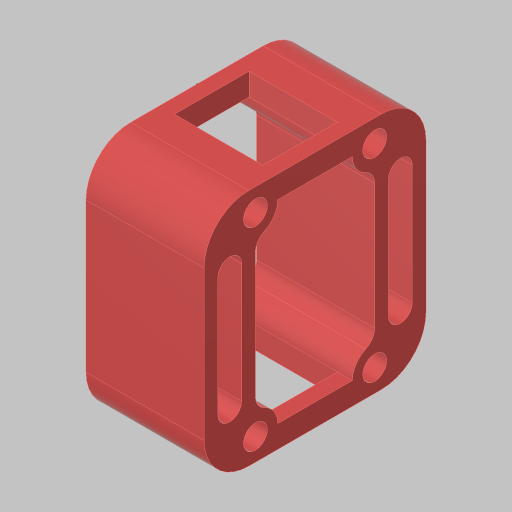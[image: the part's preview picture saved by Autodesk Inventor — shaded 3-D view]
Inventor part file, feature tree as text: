
AUTODESK INVENTOR PART (.ipt)
format: ipt  version: 2023.5 (Build 275446000, 446)  size: 202,752 bytes
history: native  units: in
note: dims shown in document units (in); Inventor stores cm internally (conversion verified against a paired STEP export)
features: sketch x3, extrude x2, fillet x2, hole x1
ambient origin geometry x8: Origin, YZ Plane, XZ Plane, XY Plane, X Axis, Y Axis, Z Axis, Center Point
bodies: Solid1 (feature_tree)
feature tree (8):
  sketch  "Sketch1"  dims[d0=1.0in d1=1.625in]
  extrude  "Extrusion1"  Depth=1.625in
  hole  "Hole1"  [1 undecoded]
  sketch  "Sketch2"  dims[d2=0.375in d3=1.86in]
  extrude  "Extrusion2"  Depth=1.0in
  fillet  "Fillet1"  Radius=0.99in
  fillet  "Fillet2"  Radius=0.125in
  sketch  "Sketch3"  dims[d4=0.1in d5=1.0in d6=0.99in d7=0.0in d8=0.201in d9=0.75in d10=0.385in d11=0.25in d12=0.5635in d13=1.0in d14=0.8108in d16=0.125in d17=0.1253in d19=0.0in d20=0.0in d21=0.125in d22=0.375in]
note: 1 required parameter value undecoded (feature->parameter linkage not recoverable at this tier; creation-order binding heuristic only, values carry confidence <= 0.55)
